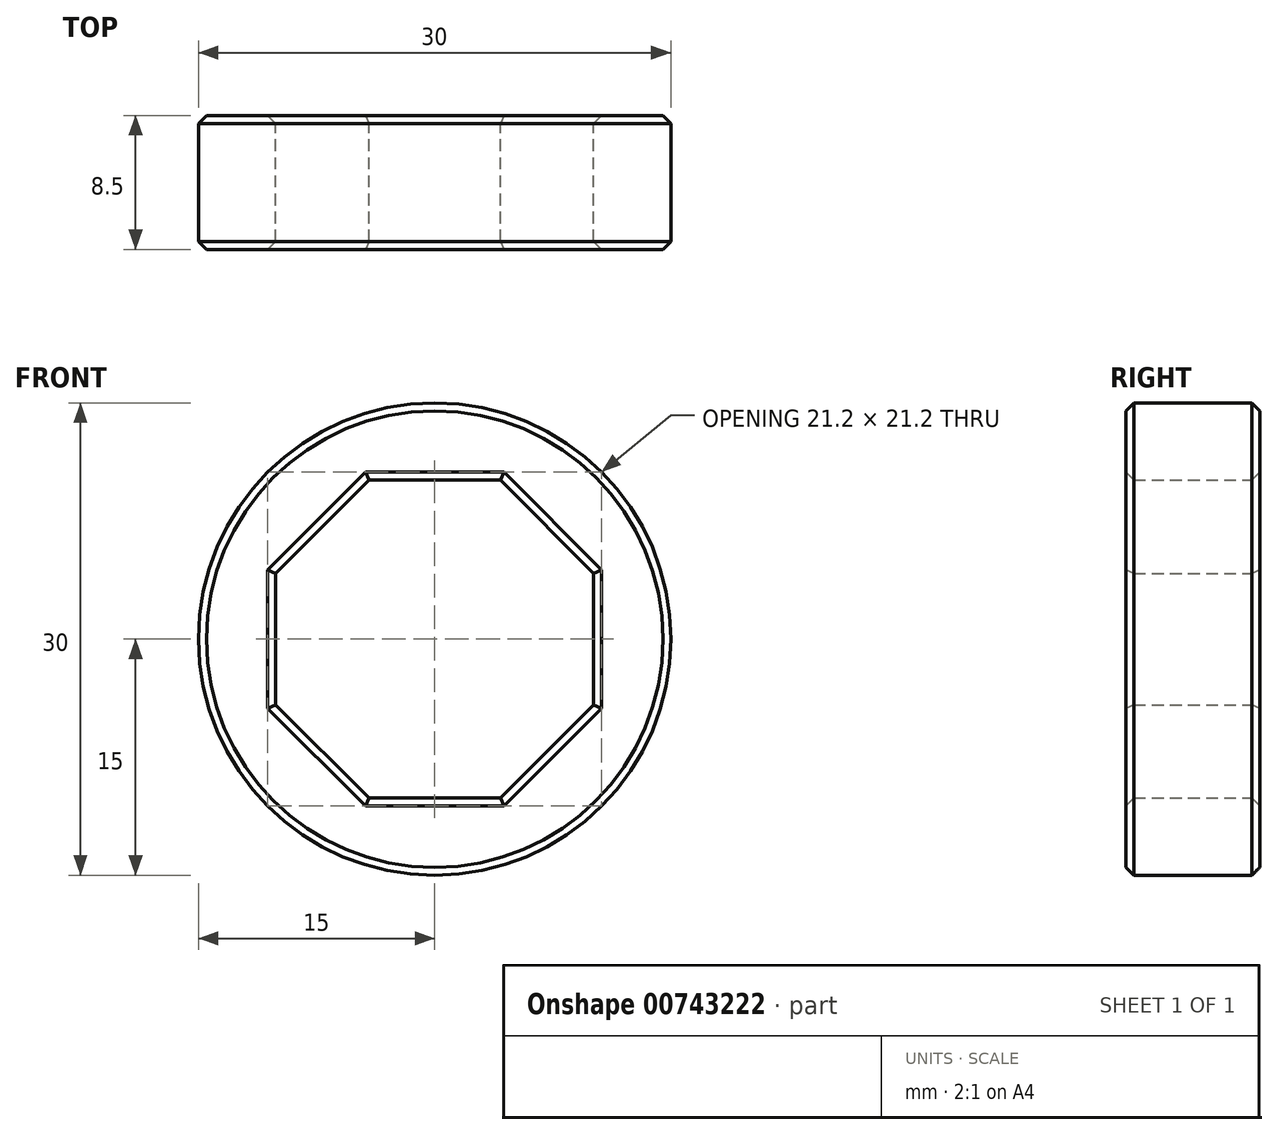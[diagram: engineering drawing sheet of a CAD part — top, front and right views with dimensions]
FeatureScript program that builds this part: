
annotation { "Feature Type Name" : "Feature", "Feature Type Description" : "" }
export const myFeature = defineFeature(function(context is Context, id is Id, definition is map)
    precondition{}
    {
        {
            var Q0;
            Q0=qCreatedBy(makeId("Front.planeOp"),FACE);
            var sketch = newSketch(context, id + "F0", { "sketchPlane" : qUnion([Q0])});
            skCircle(sketch, "E0", {"center": v(0, 0) * mm, "radius": 15 * mm});
            skCircle(sketch, "E1.cCircle", {"center": v(0, 0) * mm, "radius": 10.1 * mm, "construction": true});
            skLineSegment(sketch, "E1.0", {"start": v(-10.1, -4.18) * mm, "end": v(-10.1, 4.18) * mm});
            skLineSegment(sketch, "E1.1", {"start": v(-10.1, 4.18) * mm, "end": v(-4.18, 10.1) * mm});
            skLineSegment(sketch, "E1.2", {"start": v(-4.18, 10.1) * mm, "end": v(4.18, 10.1) * mm});
            skLineSegment(sketch, "E1.3", {"start": v(4.18, 10.1) * mm, "end": v(10.1, 4.18) * mm});
            skLineSegment(sketch, "E1.4", {"start": v(10.1, 4.18) * mm, "end": v(10.1, -4.18) * mm});
            skLineSegment(sketch, "E1.5", {"start": v(10.1, -4.18) * mm, "end": v(4.18, -10.1) * mm});
            skLineSegment(sketch, "E1.6", {"start": v(4.18, -10.1) * mm, "end": v(-4.18, -10.1) * mm});
            skLineSegment(sketch, "E1.7", {"start": v(-4.18, -10.1) * mm, "end": v(-10.1, -4.18) * mm});
            skPoint(sketch, "E1.0.midPoint", {"position": v(-10.1, 0) * mm});
            skSolve(sketch);
        }
        {
            var Q0;
            Q0=makeQuery(id+"F0.imprint","IMPRINT",FACE,{"disambiguationData":[TD([[makeQuery(id+"F0.imprint","IMPRINT",EDGE,{"derivedFrom":sQuery(id+"F0.wireOp",EDGE,"E0")}),1.0]])]});
            var Q1;
            Q1=sQuery(id+"F0.wireOp",EDGE,"E0");
            extrude(context, id + "F1", {"entities" : qUnion([Q0]), "surfaceEntities" : qUnion([Q1]), "depth" : (12.5 - 4) * mm, "offsetDistance" : 25 * mm});
        }
        {
            var Q0;
            Q0=makeQuery(id+"F1.opExtrude","CAP_FACE",FACE,{"disambiguationData":[OSD([sQuery(id+"F0.wireOp",EDGE,"E0"),sQuery(id+"F0.wireOp",EDGE,"E1.0"),sQuery(id+"F0.wireOp",EDGE,"E1.1"),sQuery(id+"F0.wireOp",EDGE,"E1.2"),sQuery(id+"F0.wireOp",EDGE,"E1.3"),sQuery(id+"F0.wireOp",EDGE,"E1.4"),sQuery(id+"F0.wireOp",EDGE,"E1.5"),sQuery(id+"F0.wireOp",EDGE,"E1.6"),sQuery(id+"F0.wireOp",EDGE,"E1.7")])],"isStart":false});
            var Q1;
            Q1=makeQuery(id+"F1.opExtrude","CAP_FACE",FACE,{"disambiguationData":[OSD([sQuery(id+"F0.wireOp",EDGE,"E0"),sQuery(id+"F0.wireOp",EDGE,"E1.0"),sQuery(id+"F0.wireOp",EDGE,"E1.1"),sQuery(id+"F0.wireOp",EDGE,"E1.2"),sQuery(id+"F0.wireOp",EDGE,"E1.3"),sQuery(id+"F0.wireOp",EDGE,"E1.4"),sQuery(id+"F0.wireOp",EDGE,"E1.5"),sQuery(id+"F0.wireOp",EDGE,"E1.6"),sQuery(id+"F0.wireOp",EDGE,"E1.7")])],"isStart":true});
            chamfer(context, id + "F2", {"entities" : qUnion([Q0, Q1]), "width" : 0.5 * mm, "tangentPropagation" : true});
        }
    });
